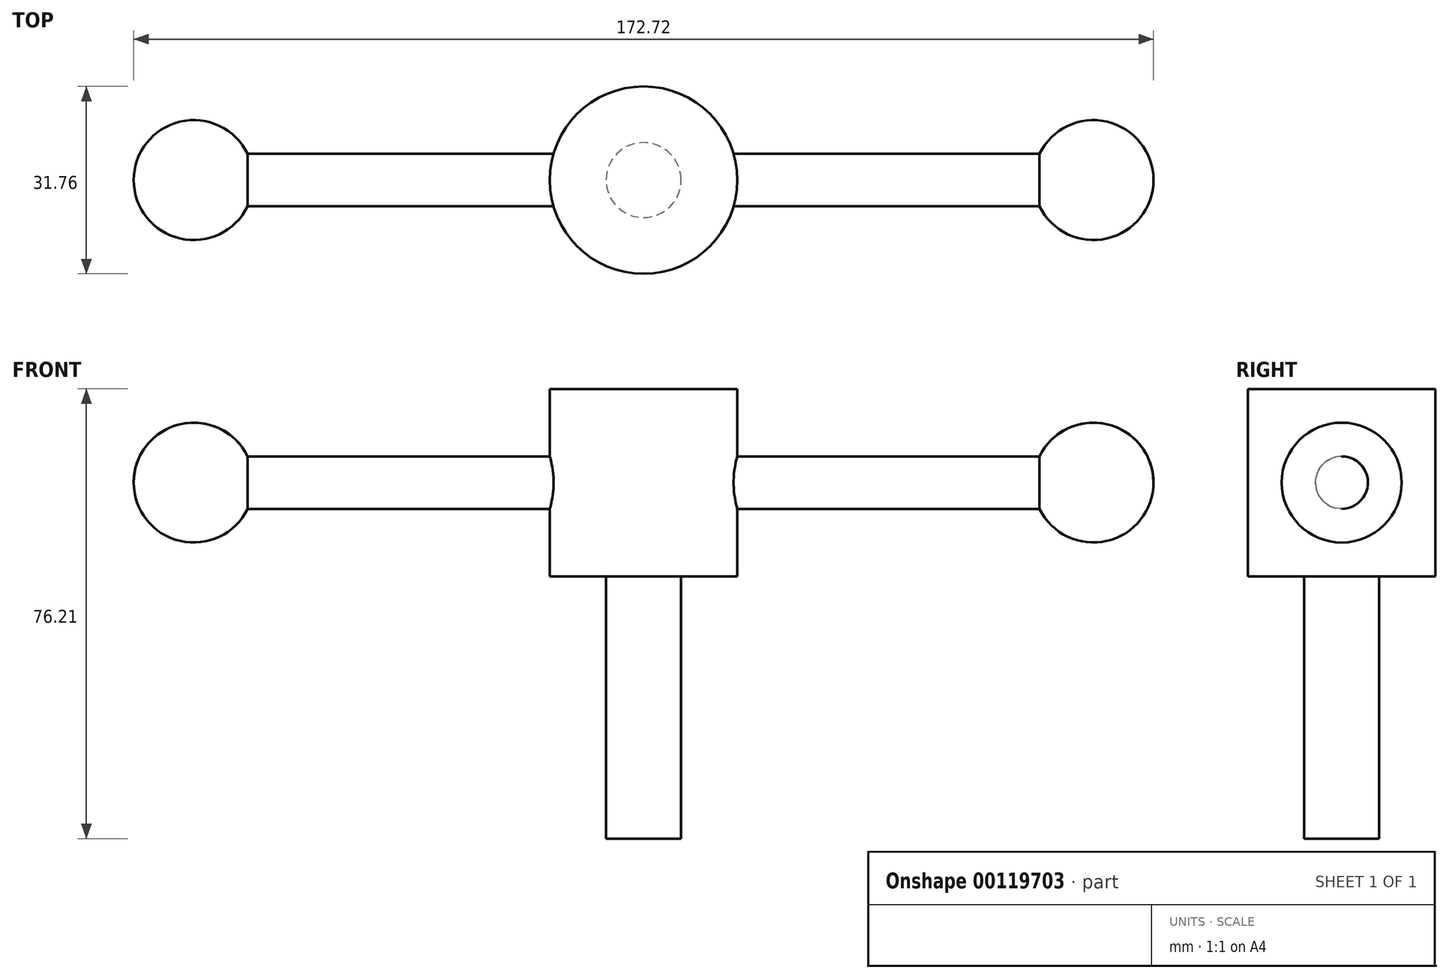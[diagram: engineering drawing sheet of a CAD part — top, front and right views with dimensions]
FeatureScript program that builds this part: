
annotation { "Feature Type Name" : "Feature", "Feature Type Description" : "" }
export const myFeature = defineFeature(function(context is Context, id is Id, definition is map)
    precondition{}
    {
        {
            var Q0;
            Q0=qCreatedBy(makeId("Top.planeOp"),FACE);
            var sketch = newSketch(context, id + "F0", { "sketchPlane" : qUnion([Q0])});
            skCircle(sketch, "E0", {"center": v(0, 0) * mm, "radius": 15.88 * mm});
            skSolve(sketch);
        }
        {
            var Q0;
            Q0 = qSketchRegion(id + "F0", true);
            extrude(context, id + "F1", {"entities" : qUnion([Q0]), "endBound" : BoundingType.SYMMETRIC, "depth" : 31.75 * mm});
        }
        {
            var Q0;
            Q0=makeQuery(id+"F1.opExtrude","CAP_FACE",FACE,{"disambiguationData":[OSD([sQuery(id+"F0.wireOp",EDGE,"E0")])],"isStart":true});
            var sketch = newSketch(context, id + "F2", { "sketchPlane" : qUnion([Q0])});
            skCircle(sketch, "E1", {"center": v(0, 0) * mm, "radius": 6.35 * mm});
            skSolve(sketch);
        }
        {
            var Q0;
            Q0 = qSketchRegion(id + "F2", true);
            extrude(context, id + "F3", {"entities" : qUnion([Q0]), "operationType" : NewBodyOperationType.ADD, "depth" : 44.45 * mm});
        }
        {
            var Q0;
            Q0=qCreatedBy(makeId("Right.planeOp"),FACE);
            var sketch = newSketch(context, id + "F4", { "sketchPlane" : qUnion([Q0])});
            skCircle(sketch, "E2", {"center": v(0, 0) * mm, "radius": 4.45 * mm});
            skSolve(sketch);
        }
        {
            var Q0;
            Q0=qCreatedBy(makeId("Right.planeOp"),FACE);
            var sketch = newSketch(context, id + "F5", { "sketchPlane" : qUnion([Q0])});
            skCircle(sketch, "E3", {"center": v(0, 0) * mm, "radius": 4.45 * mm});
            skSolve(sketch);
        }
        {
            var Q0;
            Q0 = qSketchRegion(id + "F4", true);
            extrude(context, id + "F6", {"entities" : qUnion([Q0]), "operationType" : NewBodyOperationType.REMOVE, "endBound" : BoundingType.THROUGH_ALL, "depth" : 25.4 * mm, "hasSecondDirection" : true, "secondDirectionBound" : SecondDirectionBoundingType.THROUGH_ALL, "secondDirectionOppositeDirection" : true, "secondDirectionDepth" : 25.4 * mm});
        }
        {
            var Q0;
            Q0 = qSketchRegion(id + "F5", true);
            extrude(context, id + "F7", {"entities" : qUnion([Q0]), "operationType" : NewBodyOperationType.ADD, "depth" : 76.2 * mm, "hasSecondDirection" : true, "secondDirectionOppositeDirection" : true, "secondDirectionDepth" : 76.2 * mm});
        }
        {
            var Q0;
            Q0=qCreatedBy(makeId("Front.planeOp"),FACE);
            var sketch = newSketch(context, id + "F8", { "sketchPlane" : qUnion([Q0])});
            skLineSegment(sketch, "E4", {"start": v(-86.36, 0) * mm, "end": v(86.36, 0) * mm});
            skArc(sketch, "E5", {"start": v(-66.04, 0) * mm, "mid": v(-76.2, 10.16) * mm, "end": v(-86.36, 0) * mm});
            skArc(sketch, "E6", {"start": v(86.36, 0) * mm, "mid": v(76.2, 10.16) * mm, "end": v(66.04, 0) * mm});
            skLineSegment(sketch, "E7", {"start": v(-114.76, 0) * mm, "end": v(100.34, 0) * mm, "construction": true});
            skLineSegment(sketch, "E8.bottom", {"start": v(-15.87, 0) * mm, "end": v(15.87, 0) * mm, "construction": true});
            skLineSegment(sketch, "E8.top", {"start": v(-15.87, 15.88) * mm, "end": v(15.87, 15.88) * mm, "construction": true});
            skLineSegment(sketch, "E8.left", {"start": v(-15.87, 0) * mm, "end": v(-15.87, 15.88) * mm, "construction": true});
            skLineSegment(sketch, "E8.right", {"start": v(15.88, 0) * mm, "end": v(15.88, 15.88) * mm, "construction": true});
            skLineSegment(sketch, "E9", {"start": v(0, 40.58) * mm, "end": v(0, -59.24) * mm, "construction": true});
            skLineSegment(sketch, "E10", {"start": v(0, 15.88) * mm, "end": v(0, -6.62) * mm, "construction": true});
            skPoint(sketch, "E10.endSnap0", {"position": v(0, 0) * mm});
            skSolve(sketch);
        }
        {
            var Q0;
            {var subQ0=sQuery(id+"F8.wireOp",EDGE,"E5");Q0=makeQuery(id+"F8.imprint","IMPRINT",FACE,{"disambiguationData":[TD([[makeQuery(id+"F8.imprint","IMPRINT",EDGE,{"derivedFrom":subQ0}),1.0]])]});}
            var Q1;
            {var subQ0=sQuery(id+"F8.wireOp",EDGE,"E6");Q1=makeQuery(id+"F8.imprint","IMPRINT",FACE,{"disambiguationData":[TD([[makeQuery(id+"F8.imprint","IMPRINT",EDGE,{"derivedFrom":subQ0}),1.0]])]});}
            var Q2;
            Q2=sQuery(id+"F8.wireOp",EDGE,"E7");
            revolve(context, id + "F9", {"operationType" : NewBodyOperationType.ADD, "entities" : qUnion([Q0, Q1]), "axis" : qUnion([Q2]), "revolveType" : RevolveType.FULL});
        }
    });
